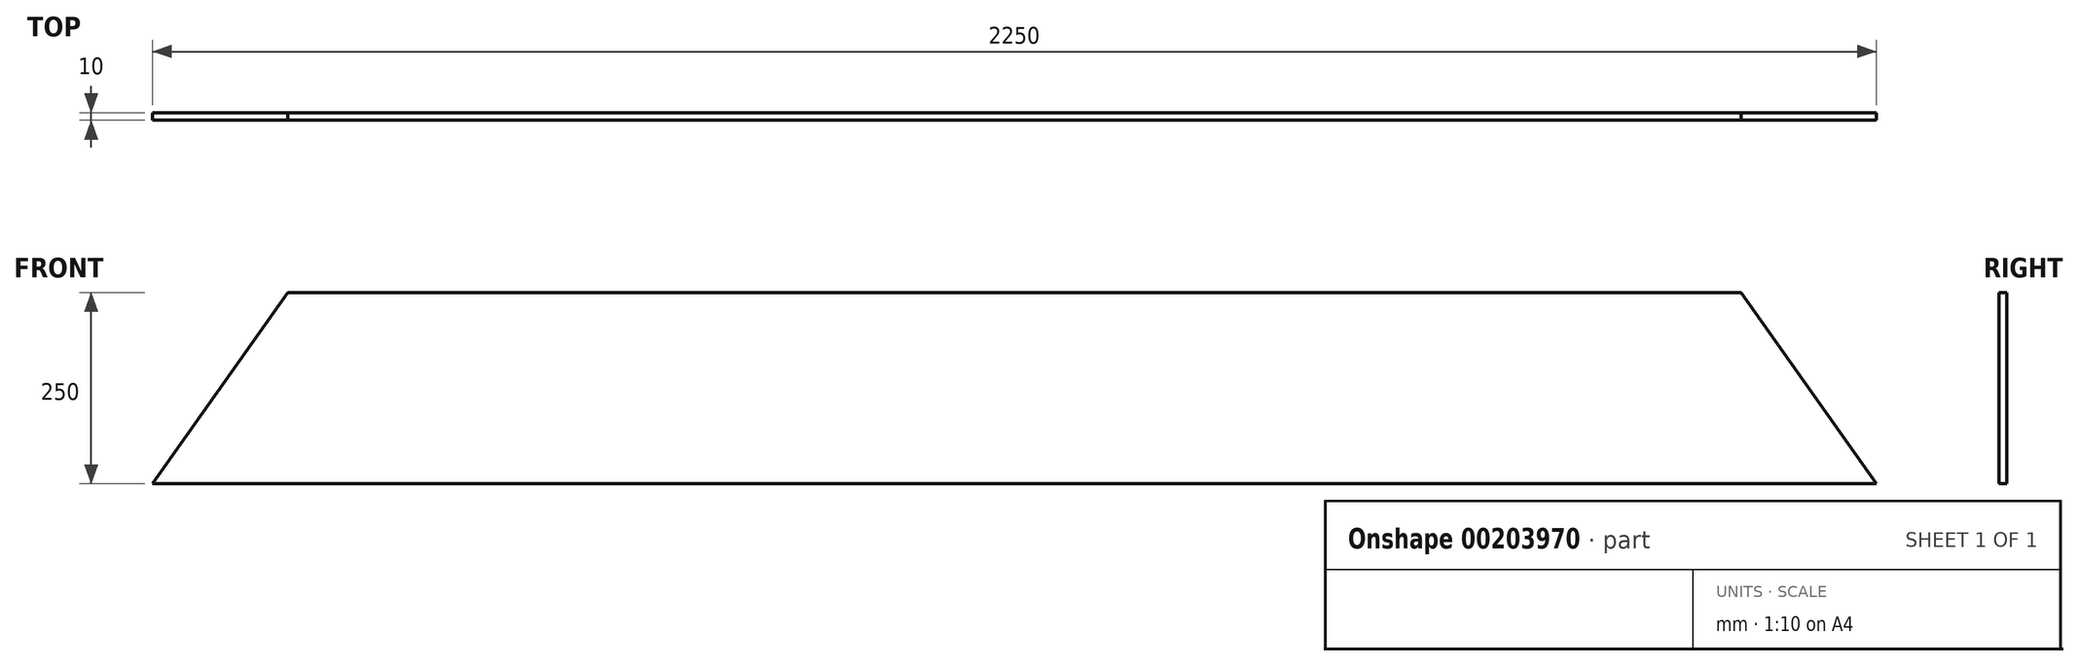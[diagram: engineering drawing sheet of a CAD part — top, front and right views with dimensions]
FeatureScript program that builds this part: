
annotation { "Feature Type Name" : "Feature", "Feature Type Description" : "" }
export const myFeature = defineFeature(function(context is Context, id is Id, definition is map)
    precondition{}
    {
        {
            var Q0;
            Q0=qCreatedBy(makeId("Front.planeOp"),FACE);
            var sketch = newSketch(context, id + "F0", { "sketchPlane" : qUnion([Q0])});
            skLineSegment(sketch, "E0", {"start": v(0, 0) * mm, "end": v(-1125, 0) * mm});
            skLineSegment(sketch, "E1", {"start": v(-1125, 0) * mm, "end": v(-948.25, 250) * mm});
            skLineSegment(sketch, "E2", {"start": v(-948.25, 250) * mm, "end": v(0, 250) * mm});
            skLineSegment(sketch, "E3", {"start": v(0, 0) * mm, "end": v(0, 668.09) * mm, "construction": true});
            skLineSegment(sketch, "E4.MirrorCS", {"start": v(948.25, 250) * mm, "end": v(0, 250) * mm});
            skLineSegment(sketch, "E5.MirrorCS", {"start": v(0, 0) * mm, "end": v(1125, 0) * mm});
            skLineSegment(sketch, "E6.MirrorCS", {"start": v(1125, 0) * mm, "end": v(948.25, 250) * mm});
            skSolve(sketch);
        }
        {
            var Q0;
            Q0 = qSketchRegion(id + "F0", true);
            extrude(context, id + "F1", {"entities" : qUnion([Q0]), "depth" : 10 * mm});
        }
    });
